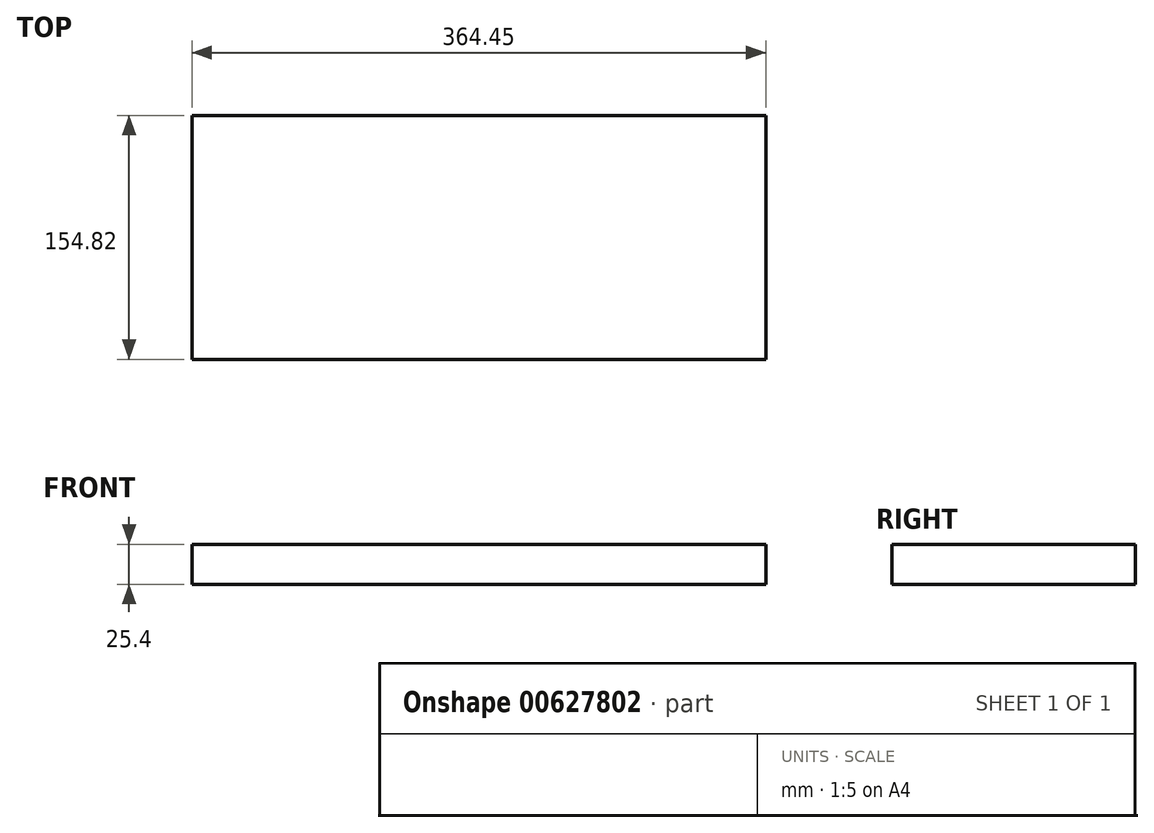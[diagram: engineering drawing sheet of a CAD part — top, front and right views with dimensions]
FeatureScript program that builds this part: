
annotation { "Feature Type Name" : "Feature", "Feature Type Description" : "" }
export const myFeature = defineFeature(function(context is Context, id is Id, definition is map)
    precondition{}
    {
        {
            var Q0;
            Q0=qCreatedBy(makeId("Top.planeOp"),FACE);
            var sketch = newSketch(context, id + "F0", { "sketchPlane" : qUnion([Q0])});
            skLineSegment(sketch, "E0", {"start": v(-75.57, 33.5) * mm, "end": v(288.88, 33.5) * mm});
            skLineSegment(sketch, "E1", {"start": v(288.88, 33.5) * mm, "end": v(288.88, -121.32) * mm});
            skLineSegment(sketch, "E2", {"start": v(288.88, -121.32) * mm, "end": v(-75.57, -121.32) * mm});
            skLineSegment(sketch, "E3", {"start": v(-75.57, -121.32) * mm, "end": v(-75.57, 33.5) * mm});
            skSolve(sketch);
        }
        {
            var Q0;
            Q0 = qSketchRegion(id + "F0", true);
            var Q1;
            Q1=makeQuery(id+"F0.imprint","IMPRINT",FACE,{"disambiguationData":[TD([[makeQuery(id+"F0.imprint","IMPRINT",EDGE,{"derivedFrom":sQuery(id+"F0.wireOp",EDGE,"E0")}),-1.0]])]});
            extrude(context, id + "F1", {"entities" : qUnion([Q0, Q1]), "depth" : 25.4 * mm, "offsetDistance" : 25.4 * mm});
        }
    });
